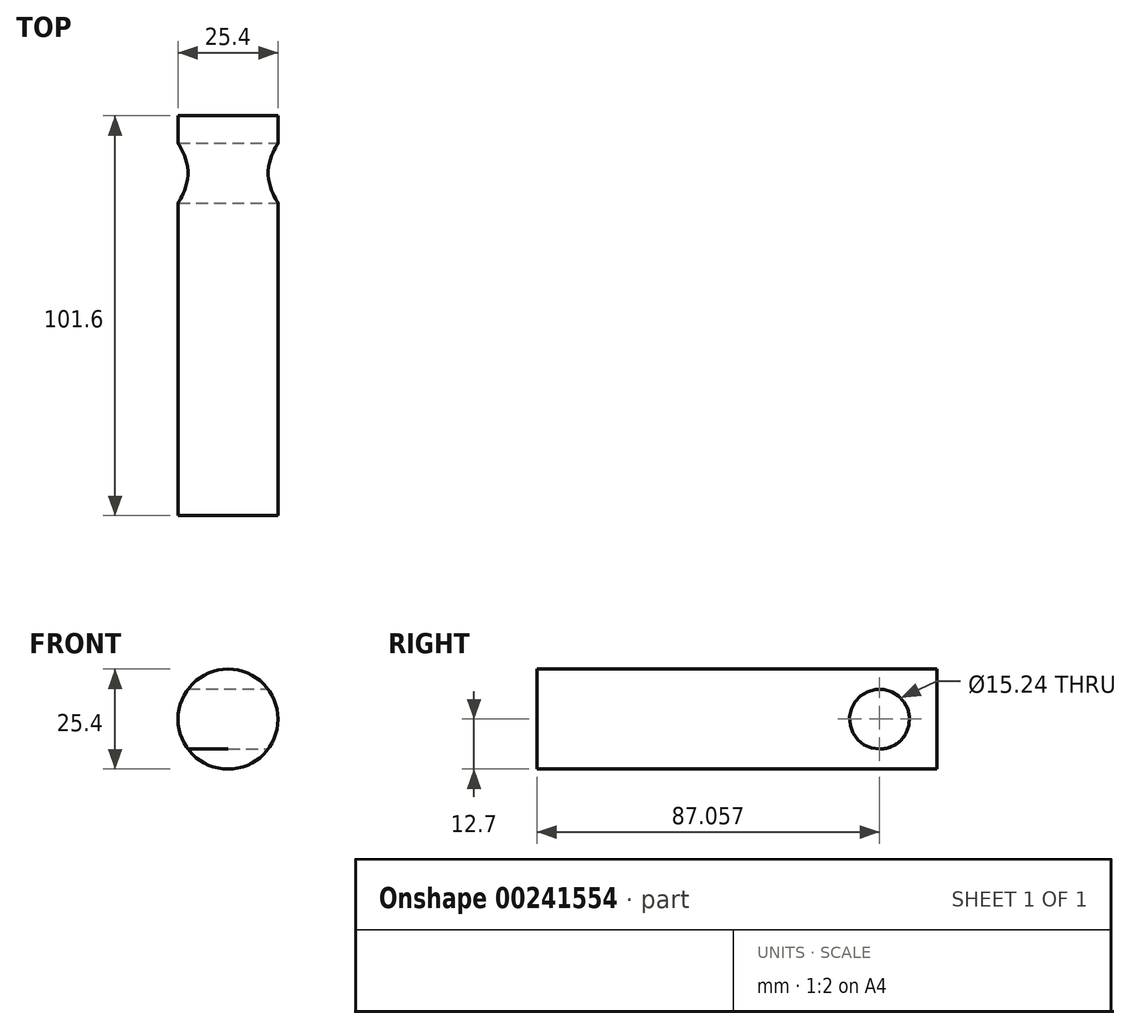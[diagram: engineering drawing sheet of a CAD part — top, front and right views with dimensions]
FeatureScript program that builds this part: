
annotation { "Feature Type Name" : "Feature", "Feature Type Description" : "" }
export const myFeature = defineFeature(function(context is Context, id is Id, definition is map)
    precondition{}
    {
        {
            var Q0;
            Q0=qCreatedBy(makeId("Front.planeOp"),FACE);
            var sketch = newSketch(context, id + "F0", { "sketchPlane" : qUnion([Q0])});
            skCircle(sketch, "E0", {"center": v(0, 0) * mm, "radius": 12.7 * mm});
            skSolve(sketch);
        }
        {
            var Q0;
            Q0=makeQuery(id+"F0.imprint","IMPRINT",FACE,{"disambiguationData":[TD([[makeQuery(id+"F0.imprint","IMPRINT",EDGE,{"derivedFrom":sQuery(id+"F0.wireOp",EDGE,"E0")}),1.0]])]});
            extrude(context, id + "F1", {"entities" : qUnion([Q0]), "depth" : 101.6 * mm});
        }
        {
            var Q0;
            Q0=qCreatedBy(makeId("Right.planeOp"),FACE);
            cPlane(context, id + "F2", {"entities" : qUnion([Q0]), "cplaneType" : CPlaneType.OFFSET, "offset" : 12.7 * mm, "width" : 152.4 * mm, "height" : 152.4 * mm});
        }
        {
            var Q0;
            Q0=qCreatedBy(id+"F2.planeOp",FACE);
            var sketch = newSketch(context, id + "F3", { "sketchPlane" : qUnion([Q0])});
            skCircle(sketch, "E1", {"center": v(-14.54, 0) * mm, "radius": 7.62 * mm});
            skSolve(sketch);
        }
        {
            var Q0;
            Q0=sQuery(id+"F3.wireOp",VERTEX,"E1.center");
            var Q1;
            Q1=makeQuery(id+"F1.opExtrude","SWEPT_BODY",BODY,{"disambiguationData":[OSD([sQuery(id+"F0.wireOp",EDGE,"E0")])]});
            hole(context, id + "F4", {"style" : HoleStyle.SIMPLE, "endStyle" : HoleEndStyle.THROUGH, "holeDiameter" : 15.24 * mm, "tappedDepth" : 12.7 * mm, "tapClearance" : 3, "locations" : qUnion([Q0]), "scope" : qUnion([Q1])});
        }
    });
